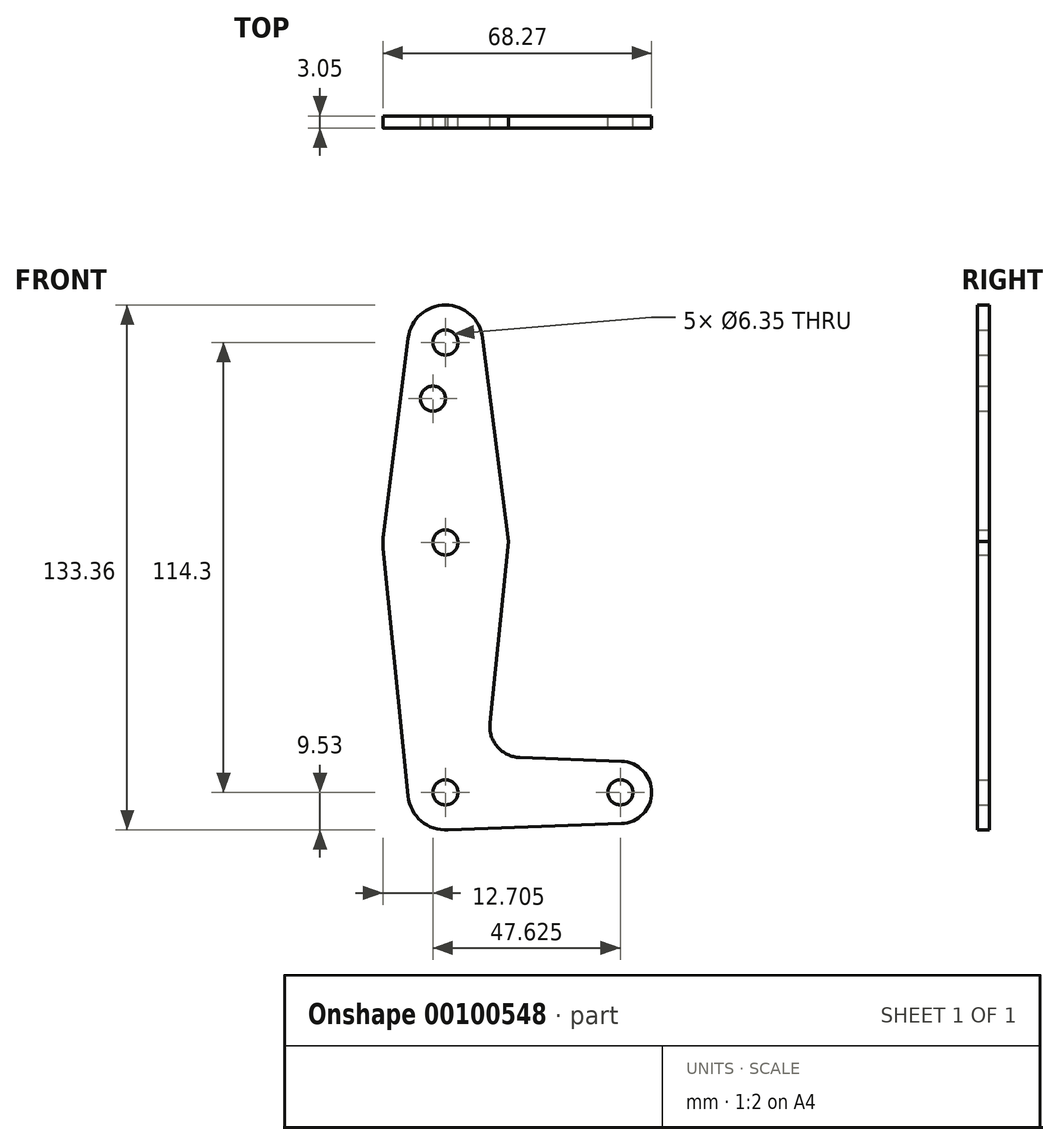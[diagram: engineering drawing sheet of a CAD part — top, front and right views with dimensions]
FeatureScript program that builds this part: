
annotation { "Feature Type Name" : "Feature", "Feature Type Description" : "" }
export const myFeature = defineFeature(function(context is Context, id is Id, definition is map)
    precondition{}
    {
        {
            var Q0;
            Q0=qCreatedBy(makeId("Front.planeOp"),FACE);
            var sketch = newSketch(context, id + "F0", { "sketchPlane" : qUnion([Q0])});
            skLineSegment(sketch, "E0", {"start": v(0, 0) * mm, "end": v(0, 114.3) * mm, "construction": true});
            skLineSegment(sketch, "E1", {"start": v(0, 0) * mm, "end": v(44.45, 0) * mm, "construction": true});
            skCircle(sketch, "E2", {"center": v(0, 114.3) * mm, "radius": 9.53 * mm});
            skCircle(sketch, "E3", {"center": v(0, 0) * mm, "radius": 9.53 * mm});
            skCircle(sketch, "E4", {"center": v(44.45, 0) * mm, "radius": 7.94 * mm});
            skLineSegment(sketch, "E5", {"start": v(-9.45, 115.5) * mm, "end": v(-15.75, 65.48) * mm});
            skLineSegment(sketch, "E6", {"start": v(9.45, 115.5) * mm, "end": v(15.98, 63.7) * mm});
            skLineSegment(sketch, "E7", {"start": v(18.93, 8.85) * mm, "end": v(44.73, 7.93) * mm});
            skLineSegment(sketch, "E8", {"start": v(0, -9.53) * mm, "end": v(44.73, -7.93) * mm});
            skPoint(sketch, "E9.orphan", {"position": v(-9.57, 0) * mm});
            skLineSegment(sketch, "E10", {"start": v(15.98, 63.7) * mm, "end": v(11.3, 17.6) * mm});
            skCircle(sketch, "E11", {"center": v(0, 63.5) * mm, "radius": 15.88 * mm});
            skLineSegment(sketch, "E12", {"start": v(-15.8, 61.91) * mm, "end": v(-9.48, -0.95) * mm});
            skCircle(sketch, "E13", {"center": v(0, 114.3) * mm, "radius": 3.18 * mm});
            skCircle(sketch, "E14", {"center": v(0, 63.5) * mm, "radius": 3.18 * mm});
            skCircle(sketch, "E15", {"center": v(0, 0) * mm, "radius": 3.18 * mm});
            skCircle(sketch, "E16", {"center": v(44.45, 0) * mm, "radius": 3.18 * mm});
            skCircle(sketch, "E17", {"center": v(-3.18, 100.03) * mm, "radius": 3.17 * mm});
            skArc(sketch, "E18.filletArc", {"start": v(11.3, 17.6) * mm, "mid": v(13.22, 11.57) * mm, "end": v(18.93, 8.85) * mm});
            skSolve(sketch);
        }
        {
            var Q0;
            Q0 = qSketchRegion(id + "F0", true);
            extrude(context, id + "F1", {"entities" : qUnion([Q0]), "depth" : 3.05 * mm});
        }
    });
